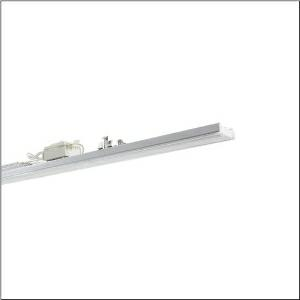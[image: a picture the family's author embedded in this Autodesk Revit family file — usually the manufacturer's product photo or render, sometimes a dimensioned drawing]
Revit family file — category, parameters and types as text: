
# Revit family: licross_11_recessed_mo_51te18dn695g
name_source: partatom
category: Lighting Fixtures
units: mm (PartAtom-declared; Revit-internal decimal feet)

## family parameters
Cut with Voids When Loaded = No
Host = Face
Light Source = No
Part Type = Normal
Room Calculation Point = No
Round Connector Dimension = Use Diameter
Shared = No

## types (1)
- --- (1 x LED, 9710 lm, 56.7 W, 6500K)
    Apparent Load = 57 VA
    CIE Flux Codes = 83 96 99 100 100
    Color Rendering = 80
    Color Temperature = 6500K
    Default Elevation = 1800 mm
    Description = Licross 11 Recessed MO, luminaire insert, of sheet steel, galvanised, coil coated, white, length: 1.500mm, width: 66mm, height: 67mm, LED rated luminous flux: 9.710lm, light colour: 865, SDCM (Standard Deviation of Colour Matching)MacAdam ≤ 2 SDCM (initial), control gear: DALI 2, with plug, 5-pole, with phase selection, mains connection: 220..240V, AC, 50/60Hz, rated input power: 57W, internal wiring halogen-free, primary light control with lens, of plastic, primary optical cover: cover, of PMMA, light emission: direct distribution, primary light characteristic: symmetric, protection rating (complete): IP54, insulation class (complete): insulation class I (protective earthing), certification: CE, ENEC, VDE, UKCA, protection symbol: D if used in an environment with non-conductive dust loads with corresponding accessories, impact resistance: IK06, permissible ambient temperature for indoor applications: -25..+35°C, corresponds to IFS (International Featured Standards) requirements for safety and quality in the food industry, reducing of maximum allowable ambient temperature of 5°C with ceiling mounting, LABS conformity tested according to VDMA 24364:2018-05, The light source and the operating device comply with the requirements of the Ecodesign Regulation (EU) 2019/2020 and are replaceable in accordance with this regulation, packaging unit: 1 piece
    Height = 58 mm
    Lamp = 1 x LED
    Lamp Light Flux = 9710 lm
    Lamp Power = 56.7 W
    Lamp count = 1
    Length = 1500 mm
    Luminous efficacy = 171 lm/W
    Manufacturer = Siteco
    ModVariant = No
    Model = 51TE18DN695G
    Mounting Place = Ceiling
    Mounting Type = Pendant
    Number of Poles = 1
    OnlyDefault = Yes
    Power Factor = 1
    Product Name = Licross 11 Recessed MO
    Product group = luminaire insert | ceiling pendant
    ProductGroupID = 901
    Protection Class = Protection class I
    Protection Degree = IP 54
    RLX_Detail_Level = 1
    RLX_Emergency_Light_Flux = 0 lm
    RLX_Emergency_Type = 0
    RLX_Emergency_Type_DB = No
    RlxData = <blob elided: 24741 chars, md5=d3a7c13a>
    Socket = socket
    Standby Power = 0 W
    System Light Flux = 9710 lm
    System Power = 57 W
    Type Comments = factory setting: luminous flux: 100 % | dim-lin: 254 | 378 mA
    Type Image = l_1296930.jpg
    URL = http://relux.com
    VarID = @adj_030245
    Voltage = 0 V
    Weight = 0.00 kg
    Width = 66 mm

## geometry (parser evidence)
native form markers: Blend x4, Sweep x9
no freeform markers — native parametric forms only
